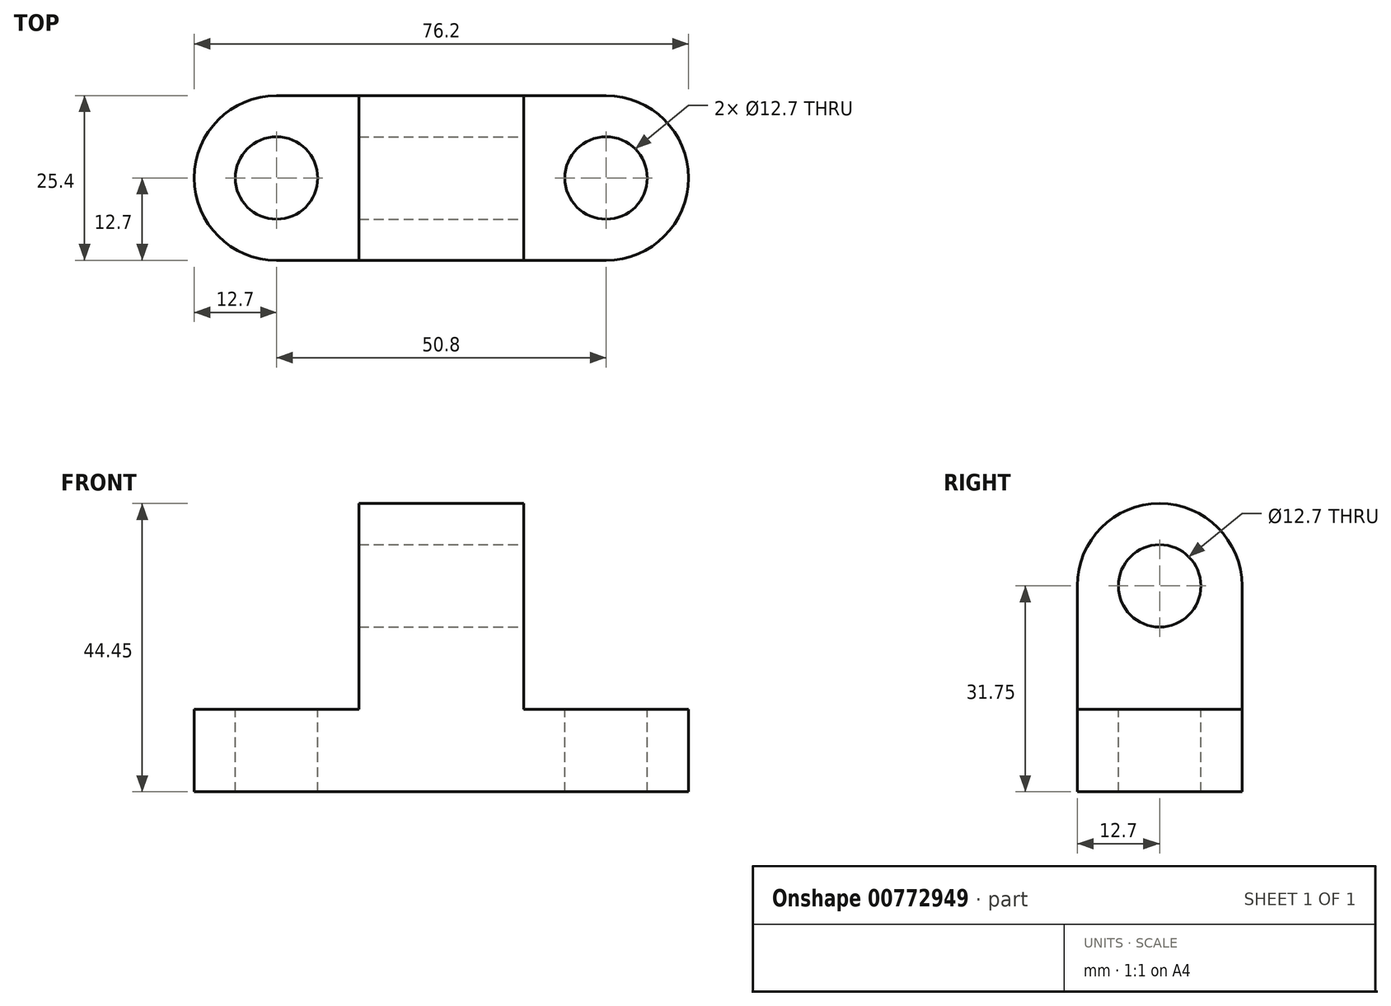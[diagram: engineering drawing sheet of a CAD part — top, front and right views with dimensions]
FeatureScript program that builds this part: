
annotation { "Feature Type Name" : "Feature", "Feature Type Description" : "" }
export const myFeature = defineFeature(function(context is Context, id is Id, definition is map)
    precondition{}
    {
        {
            var Q0;
            Q0=qCreatedBy(makeId("Front.planeOp"),FACE);
            var sketch = newSketch(context, id + "F0", { "sketchPlane" : qUnion([Q0])});
            skLineSegment(sketch, "E0", {"start": v(0, 0) * mm, "end": v(76.2, 0) * mm});
            skLineSegment(sketch, "E1", {"start": v(76.2, 0) * mm, "end": v(76.2, 44.45) * mm});
            skLineSegment(sketch, "E2", {"start": v(76.2, 44.45) * mm, "end": v(0, 44.45) * mm});
            skLineSegment(sketch, "E3", {"start": v(0, 44.45) * mm, "end": v(0, 0) * mm});
            skSolve(sketch);
        }
        {
            var Q0;
            Q0=makeQuery(id+"F0.imprint","IMPRINT",FACE,{"disambiguationData":[TD([[makeQuery(id+"F0.imprint","IMPRINT",EDGE,{"derivedFrom":sQuery(id+"F0.wireOp",EDGE,"E0")}),1.0]])]});
            extrude(context, id + "F1", {"entities" : qUnion([Q0]), "depth" : 25.4 * mm, "offsetDistance" : 25.4 * mm});
        }
        {
            var Q0;
            Q0=makeQuery(id+"F1.opExtrude","CAP_FACE",FACE,{"disambiguationData":[OSD([sQuery(id+"F0.wireOp",EDGE,"E0"),sQuery(id+"F0.wireOp",EDGE,"E1"),sQuery(id+"F0.wireOp",EDGE,"E2"),sQuery(id+"F0.wireOp",EDGE,"E3")])],"isStart":false});
            var sketch = newSketch(context, id + "F2", { "sketchPlane" : qUnion([Q0])});
            skLineSegment(sketch, "E4", {"start": v(50.8, 44.45) * mm, "end": v(50.8, 12.7) * mm});
            skLineSegment(sketch, "E5", {"start": v(50.8, 12.7) * mm, "end": v(76.2, 12.7) * mm});
            skLineSegment(sketch, "E6", {"start": v(25.4, 44.45) * mm, "end": v(25.4, 12.7) * mm});
            skLineSegment(sketch, "E7", {"start": v(25.4, 12.7) * mm, "end": v(0, 12.7) * mm});
            skSolve(sketch);
        }
        {
            var Q0;
            {var subQ0=sQuery(id+"F2.wireOp",EDGE,"E6");Q0=makeQuery(id+"F2.imprint","IMPRINT",FACE,{"disambiguationData":[TD([[makeQuery(id+"F2.imprint","IMPRINT",EDGE,{"derivedFrom":subQ0}),-1.0]])]});}
            var Q1;
            {var subQ0=sQuery(id+"F2.wireOp",EDGE,"E4");Q1=makeQuery(id+"F2.imprint","IMPRINT",FACE,{"disambiguationData":[TD([[makeQuery(id+"F2.imprint","IMPRINT",EDGE,{"derivedFrom":subQ0}),1.0]])]});}
            extrude(context, id + "F3", {"entities" : qUnion([Q0, Q1]), "operationType" : NewBodyOperationType.REMOVE, "oppositeDirection" : true, "depth" : 25.4 * mm, "offsetDistance" : 25.4 * mm});
        }
        {
            var Q0;
            Q0=makeQuery(id+"F3.boolean.opBoolean","COPY",FACE,{"derivedFrom":makeQuery(id+"F3.opExtrude","SWEPT_FACE",FACE,{"disambiguationData":[OSD([sQuery(id+"F2.wireOp",EDGE,"E5")])]})});
            var sketch = newSketch(context, id + "F4", { "sketchPlane" : qUnion([Q0])});
            skCircle(sketch, "E8", {"center": v(63.5, -12.7) * mm, "radius": 6.35 * mm});
            skCircle(sketch, "E9", {"center": v(12.7, -12.7) * mm, "radius": 6.35 * mm});
            skSolve(sketch);
        }
        {
            var Q0;
            Q0=makeQuery(id+"F4.imprint","IMPRINT",FACE,{"disambiguationData":[TD([[makeQuery(id+"F4.imprint","IMPRINT",EDGE,{"derivedFrom":sQuery(id+"F4.wireOp",EDGE,"E9")}),1.0]])]});
            var Q1;
            Q1=makeQuery(id+"F4.imprint","IMPRINT",FACE,{"disambiguationData":[TD([[makeQuery(id+"F4.imprint","IMPRINT",EDGE,{"derivedFrom":sQuery(id+"F4.wireOp",EDGE,"E8")}),1.0]])]});
            extrude(context, id + "F5", {"entities" : qUnion([Q0, Q1]), "operationType" : NewBodyOperationType.REMOVE, "oppositeDirection" : true, "depth" : 25.4 * mm, "offsetDistance" : 25.4 * mm});
        }
        {
            var Q0;
            Q0=makeQuery(id+"F3.boolean.opBoolean","COPY",FACE,{"derivedFrom":makeQuery(id+"F3.opExtrude","SWEPT_FACE",FACE,{"disambiguationData":[OSD([sQuery(id+"F2.wireOp",EDGE,"E5")])]})});
            var sketch = newSketch(context, id + "F6", { "sketchPlane" : qUnion([Q0])});
            skArc(sketch, "E10", {"start": v(63.5, -25.4) * mm, "mid": v(76.2, -12.7) * mm, "end": v(63.5, 0) * mm});
            skLineSegment(sketch, "E11.0", {"start": v(25.4, 0) * mm, "end": v(0, 0) * mm});
            skLineSegment(sketch, "E12.0.0", {"start": v(0, -25.4) * mm, "end": v(25.4, -25.4) * mm});
            skLineSegment(sketch, "E12.0.1", {"start": v(25.4, -25.4) * mm, "end": v(25.4, 0) * mm});
            skLineSegment(sketch, "E12.0.3", {"start": v(0, 0) * mm, "end": v(0, -25.4) * mm});
            skArc(sketch, "E13", {"start": v(12.7, 0) * mm, "mid": v(0, -12.7) * mm, "end": v(12.7, -25.4) * mm});
            skSolve(sketch);
        }
        {
            var Q0;
            {var subQ0=sQuery(id+"F6.wireOp",EDGE,"E10");var subQ1=sQuery(id+"F2.wireOp",EDGE,"E5");var subQ2=makeQuery(id+"F3.boolean.opBoolean","COPY",EDGE,{"derivedFrom":makeQuery(id+"F3.opExtrude","CAP_EDGE",EDGE,{"disambiguationData":[OSD([subQ1])],"isStart":false})});var subQ3=makeQuery(id+"F6.imprint","INTERSECT",VERTEX,{"derivedFrom":[subQ2,subQ0]});Q0=makeQuery(id+"F6.imprint","IMPRINT",FACE,{"disambiguationData":[TD([[makeQuery(id+"F6.imprint","IMPRINT",EDGE,{"disambiguationData":[TD([[subQ3,1.0]])],"derivedFrom":subQ0}),-1.0]])]});}
            var Q1;
            {var subQ0=sQuery(id+"F6.wireOp",EDGE,"E10");var subQ1=sQuery(id+"F2.wireOp",EDGE,"E5");var subQ2=makeQuery(id+"F3.boolean.opBoolean","COPY",EDGE,{"derivedFrom":makeQuery(id+"F3.opExtrude","CAP_EDGE",EDGE,{"disambiguationData":[OSD([subQ1])],"isStart":true})});var subQ3=makeQuery(id+"F6.imprint","INTERSECT",VERTEX,{"derivedFrom":[subQ2,subQ0]});Q1=makeQuery(id+"F6.imprint","IMPRINT",FACE,{"disambiguationData":[TD([[makeQuery(id+"F6.imprint","IMPRINT",EDGE,{"disambiguationData":[TD([[subQ3,-1.0]])],"derivedFrom":subQ0}),-1.0]])]});}
            var Q2;
            {var subQ0=sQuery(id+"F6.wireOp",EDGE,"E12.0.3");var subQ1=sQuery(id+"F6.wireOp",EDGE,"E12.0.0");var subQ2=makeQuery(id+"F6.imprint","INTERSECT",VERTEX,{"derivedFrom":[subQ1,subQ0]});Q2=makeQuery(id+"F6.imprint","IMPRINT",FACE,{"disambiguationData":[TD([[makeQuery(id+"F6.imprint","IMPRINT",EDGE,{"disambiguationData":[TD([[subQ2,-1.0]])],"derivedFrom":subQ1}),1.0]])]});}
            var Q3;
            {var subQ0=sQuery(id+"F6.wireOp",EDGE,"E12.0.3");var subQ1=sQuery(id+"F6.wireOp",EDGE,"E11.0");var subQ2=makeQuery(id+"F6.imprint","INTERSECT",VERTEX,{"derivedFrom":[subQ1,subQ0]});Q3=makeQuery(id+"F6.imprint","IMPRINT",FACE,{"disambiguationData":[TD([[makeQuery(id+"F6.imprint","IMPRINT",EDGE,{"disambiguationData":[TD([[subQ2,1.0]])],"derivedFrom":subQ1}),1.0]])]});}
            extrude(context, id + "F7", {"entities" : qUnion([Q0, Q1, Q2, Q3]), "operationType" : NewBodyOperationType.REMOVE, "oppositeDirection" : true, "depth" : 25.4 * mm, "offsetDistance" : 25.4 * mm});
        }
        {
            var Q0;
            Q0=makeQuery(id+"F3.boolean.opBoolean","COPY",FACE,{"derivedFrom":makeQuery(id+"F3.opExtrude","SWEPT_FACE",FACE,{"disambiguationData":[OSD([sQuery(id+"F2.wireOp",EDGE,"E4")])]})});
            var sketch = newSketch(context, id + "F8", { "sketchPlane" : qUnion([Q0])});
            skCircle(sketch, "E14", {"center": v(-12.7, 31.75) * mm, "radius": 6.35 * mm});
            skSolve(sketch);
        }
        {
            var Q0;
            Q0=makeQuery(id+"F8.imprint","IMPRINT",FACE,{"disambiguationData":[TD([[makeQuery(id+"F8.imprint","IMPRINT",EDGE,{"derivedFrom":sQuery(id+"F8.wireOp",EDGE,"E14")}),1.0]])]});
            extrude(context, id + "F9", {"entities" : qUnion([Q0]), "operationType" : NewBodyOperationType.REMOVE, "oppositeDirection" : true, "depth" : 25.4 * mm, "offsetDistance" : 25.4 * mm});
        }
        {
            var Q0;
            Q0=makeQuery(id+"F3.boolean.opBoolean","COPY",FACE,{"derivedFrom":makeQuery(id+"F3.opExtrude","SWEPT_FACE",FACE,{"disambiguationData":[OSD([sQuery(id+"F2.wireOp",EDGE,"E4")])]})});
            var sketch = newSketch(context, id + "F10", { "sketchPlane" : qUnion([Q0])});
            skArc(sketch, "E15", {"start": v(0, 31.75) * mm, "mid": v(-12.7, 44.45) * mm, "end": v(-25.4, 31.75) * mm});
            skSolve(sketch);
        }
        {
            var Q0;
            Q0 = qSketchRegion(id + "F10", true);
            var Q1;
            {var subQ0=sQuery(id+"F10.wireOp",EDGE,"E15");var subQ1=sQuery(id+"F2.wireOp",EDGE,"E4");var subQ2=makeQuery(id+"F3.boolean.opBoolean","COPY",EDGE,{"derivedFrom":makeQuery(id+"F3.opExtrude","CAP_EDGE",EDGE,{"disambiguationData":[OSD([subQ1])],"isStart":true})});var subQ3=makeQuery(id+"F10.imprint","INTERSECT",VERTEX,{"derivedFrom":[subQ2,subQ0]});Q1=makeQuery(id+"F10.imprint","IMPRINT",FACE,{"disambiguationData":[TD([[makeQuery(id+"F10.imprint","IMPRINT",EDGE,{"disambiguationData":[TD([[subQ3,1.0]])],"derivedFrom":subQ0}),-1.0]])]});}
            var Q2;
            {var subQ0=sQuery(id+"F10.wireOp",EDGE,"E15");var subQ1=sQuery(id+"F2.wireOp",EDGE,"E4");var subQ2=makeQuery(id+"F3.boolean.opBoolean","COPY",EDGE,{"derivedFrom":makeQuery(id+"F3.opExtrude","CAP_EDGE",EDGE,{"disambiguationData":[OSD([subQ1])],"isStart":false})});var subQ3=makeQuery(id+"F10.imprint","INTERSECT",VERTEX,{"derivedFrom":[subQ2,subQ0]});Q2=makeQuery(id+"F10.imprint","IMPRINT",FACE,{"disambiguationData":[TD([[makeQuery(id+"F10.imprint","IMPRINT",EDGE,{"disambiguationData":[TD([[subQ3,-1.0]])],"derivedFrom":subQ0}),-1.0]])]});}
            extrude(context, id + "F11", {"entities" : qUnion([Q0, Q1, Q2]), "operationType" : NewBodyOperationType.REMOVE, "oppositeDirection" : true, "depth" : 25.4 * mm, "offsetDistance" : 25.4 * mm});
        }
    });
